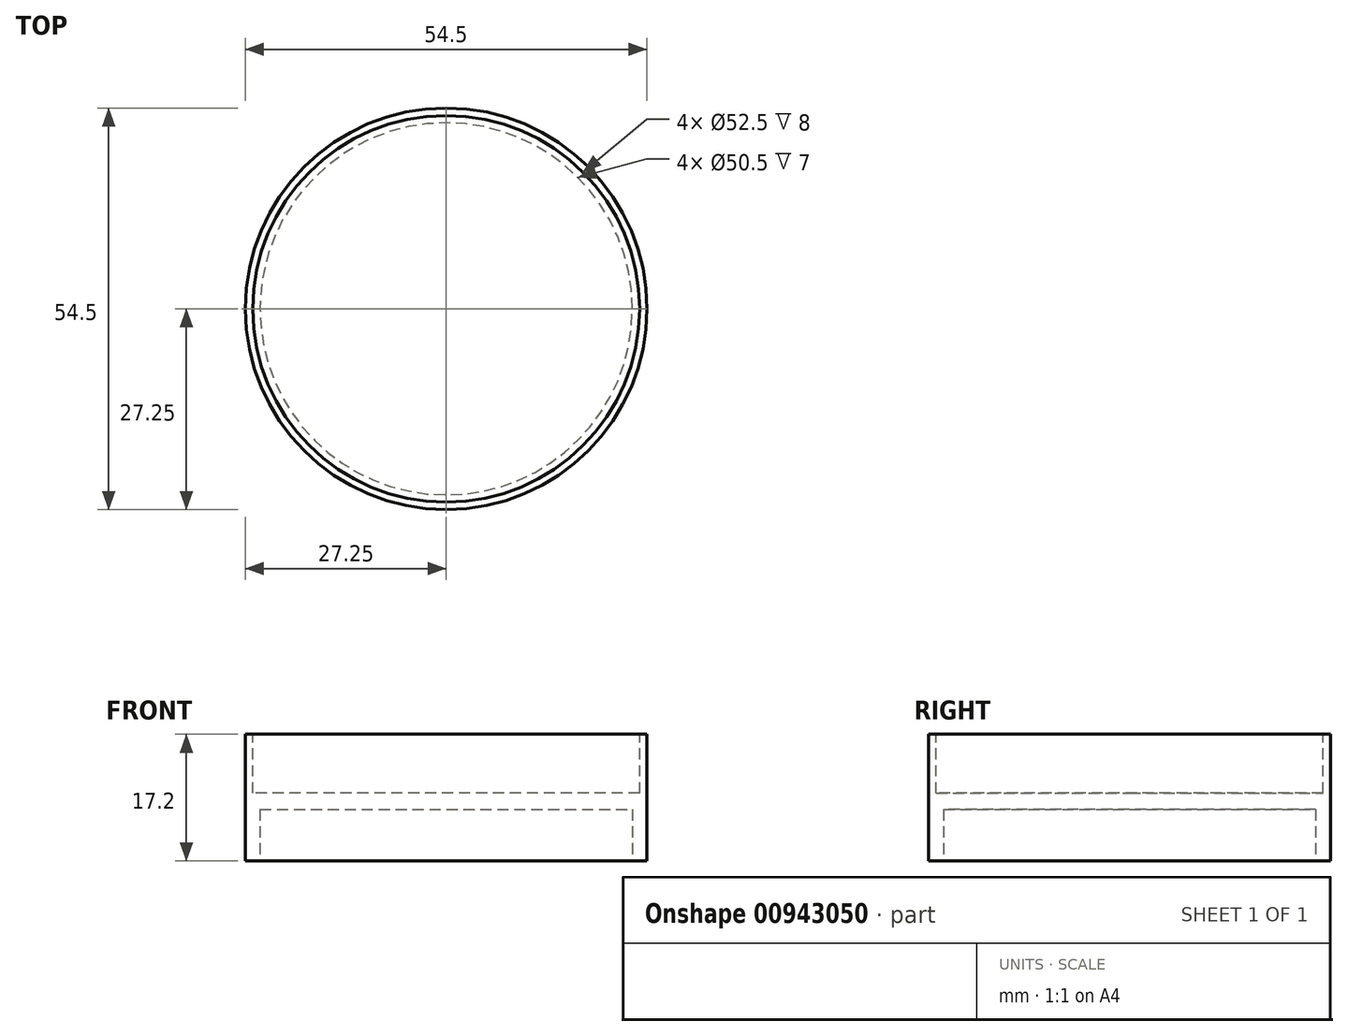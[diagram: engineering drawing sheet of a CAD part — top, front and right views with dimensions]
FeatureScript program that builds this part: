
annotation { "Feature Type Name" : "Feature", "Feature Type Description" : "" }
export const myFeature = defineFeature(function(context is Context, id is Id, definition is map)
    precondition{}
    {
        {
            var Q0;
            Q0=qCreatedBy(makeId("Top.planeOp"),FACE);
            var sketch = newSketch(context, id + "F0", { "sketchPlane" : qUnion([Q0])});
            skCircle(sketch, "E0", {"center": v(0, 0) * mm, "radius": 27.25 * mm});
            skSolve(sketch);
        }
        {
            var Q0;
            Q0 = qSketchRegion(id + "F0", true);
            extrude(context, id + "F1", {"entities" : qUnion([Q0]), "endBound" : BoundingType.SYMMETRIC, "depth" : 17.2 * mm, "offsetDistance" : 25 * mm});
        }
        {
            var Q0;
            Q0=makeQuery(id+"F1.opExtrude","CAP_FACE",FACE,{"disambiguationData":[OSD([sQuery(id+"F0.wireOp",EDGE,"E0")])],"isStart":false});
            var sketch = newSketch(context, id + "F2", { "sketchPlane" : qUnion([Q0])});
            skCircle(sketch, "E1", {"center": v(0, 0) * mm, "radius": 26.25 * mm});
            skSolve(sketch);
        }
        {
            var Q0;
            Q0 = qSketchRegion(id + "F2", true);
            extrude(context, id + "F3", {"entities" : qUnion([Q0]), "operationType" : NewBodyOperationType.REMOVE, "oppositeDirection" : true, "depth" : 8 * mm, "offsetDistance" : 25 * mm});
        }
        {
            var Q0;
            Q0=makeQuery(id+"F1.opExtrude","CAP_FACE",FACE,{"disambiguationData":[OSD([sQuery(id+"F0.wireOp",EDGE,"E0")])],"isStart":true});
            var sketch = newSketch(context, id + "F4", { "sketchPlane" : qUnion([Q0])});
            skCircle(sketch, "E2", {"center": v(0, 0) * mm, "radius": 25.25 * mm});
            skSolve(sketch);
        }
        {
            var Q0;
            Q0 = qSketchRegion(id + "F4", true);
            extrude(context, id + "F5", {"entities" : qUnion([Q0]), "operationType" : NewBodyOperationType.REMOVE, "oppositeDirection" : true, "depth" : 7 * mm, "offsetDistance" : 25 * mm});
        }
    });
